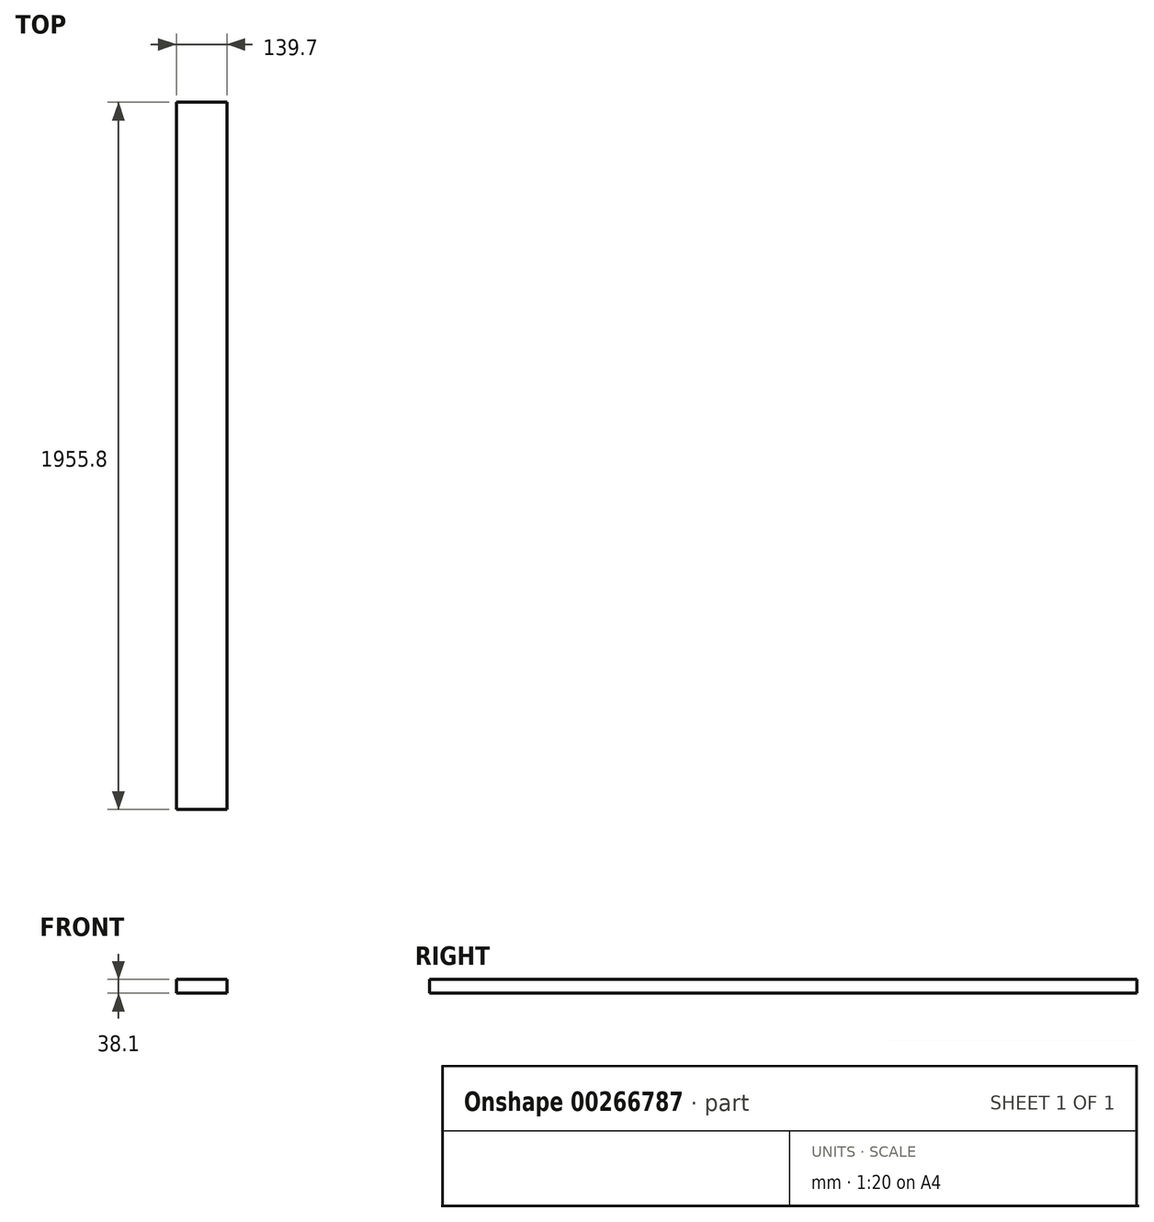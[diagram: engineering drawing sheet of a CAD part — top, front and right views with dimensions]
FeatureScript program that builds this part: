
annotation { "Feature Type Name" : "Feature", "Feature Type Description" : "" }
export const myFeature = defineFeature(function(context is Context, id is Id, definition is map)
    precondition{}
    {
        {
            var Q0;
            Q0=qCreatedBy(makeId("Front.planeOp"),FACE);
            var sketch = newSketch(context, id + "F0", { "sketchPlane" : qUnion([Q0])});
            skLineSegment(sketch, "E0.bottom", {"start": v(-48.34, 23.68) * mm, "end": v(91.36, 23.68) * mm});
            skLineSegment(sketch, "E0.top", {"start": v(-48.34, -14.42) * mm, "end": v(91.36, -14.42) * mm});
            skLineSegment(sketch, "E0.left", {"start": v(-48.34, 23.68) * mm, "end": v(-48.34, -14.42) * mm});
            skLineSegment(sketch, "E0.right", {"start": v(91.36, 23.68) * mm, "end": v(91.36, -14.42) * mm});
            skSolve(sketch);
        }
        {
            var Q0;
            Q0=qSketchRegion(id+"F0",true);
            extrude(context, id + "F1", {"entities" : qUnion([Q0]), "depth" : 1955.8 * mm});
        }
    });
